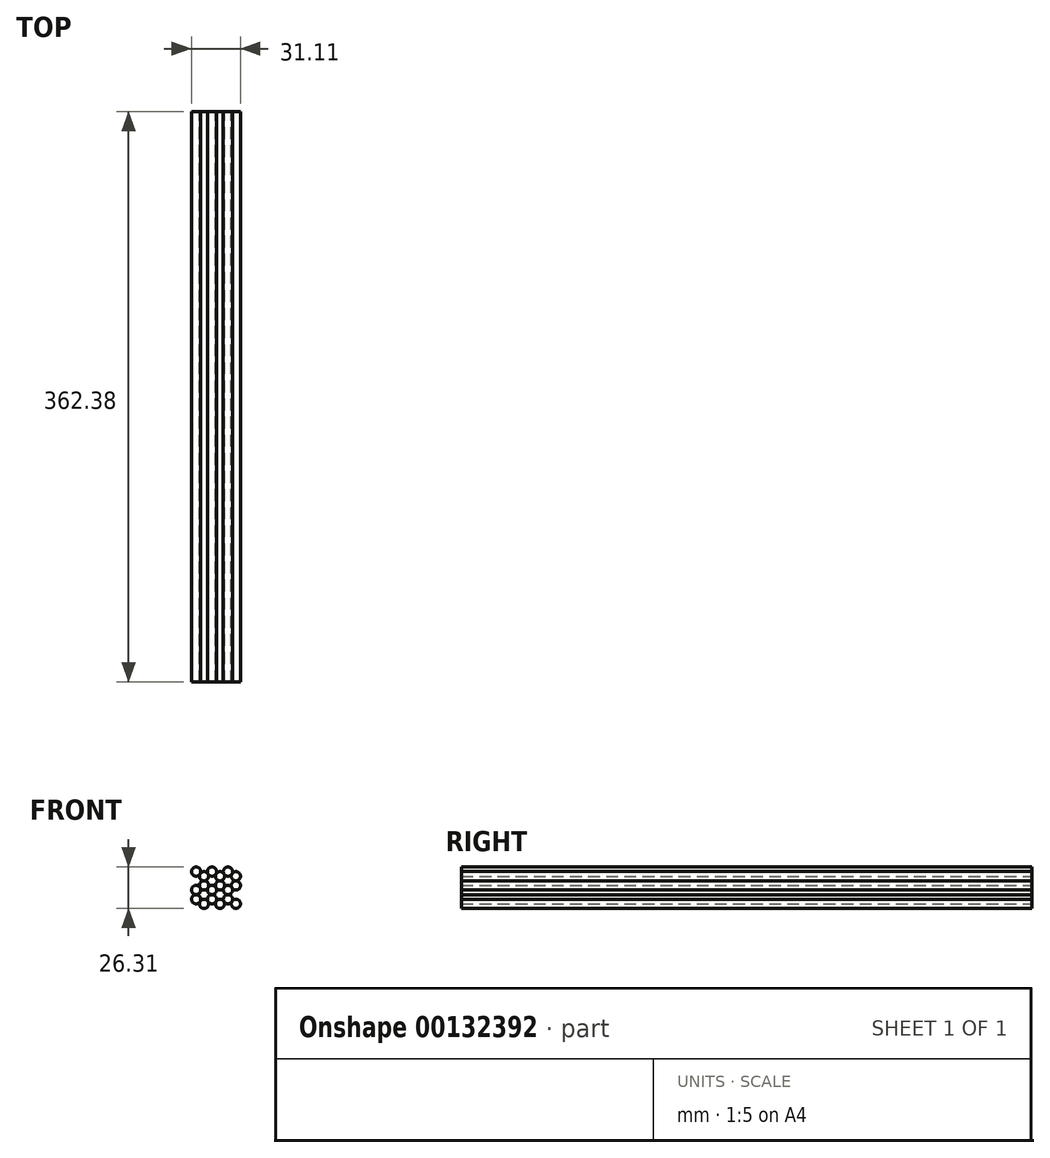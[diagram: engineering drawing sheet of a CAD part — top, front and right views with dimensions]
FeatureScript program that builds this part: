
annotation { "Feature Type Name" : "Feature", "Feature Type Description" : "" }
export const myFeature = defineFeature(function(context is Context, id is Id, definition is map)
    precondition{}
    {
        {
            var Q0;
            Q0=qCreatedBy(makeId("Front.planeOp"),FACE);
            var sketch = newSketch(context, id + "F0", { "sketchPlane" : qUnion([Q0])});
            skCircle(sketch, "E0", {"center": v(0, 0) * mm, "radius": 2.92 * mm});
            skCircle(sketch, "E1", {"center": v(5.05, -2.93) * mm, "radius": 2.92 * mm});
            skCircle(sketch, "E2", {"center": v(5.05, -8.77) * mm, "radius": 2.92 * mm});
            skCircle(sketch, "E3", {"center": v(0, -11.7) * mm, "radius": 2.92 * mm});
            skCircle(sketch, "E4", {"center": v(-5.05, -8.77) * mm, "radius": 2.92 * mm});
            skCircle(sketch, "E5", {"center": v(-5.05, -2.93) * mm, "radius": 2.92 * mm});
            skCircle(sketch, "E6", {"center": v(-10.1, 0) * mm, "radius": 2.92 * mm});
            skCircle(sketch, "E7", {"center": v(10.1, 0) * mm, "radius": 2.92 * mm});
            skCircle(sketch, "E8", {"center": v(15.16, -2.93) * mm, "radius": 2.92 * mm});
            skCircle(sketch, "E9", {"center": v(15.16, -8.77) * mm, "radius": 2.92 * mm});
            skCircle(sketch, "E10", {"center": v(10.1, -11.7) * mm, "radius": 2.92 * mm});
            skCircle(sketch, "E11", {"center": v(0, -17.54) * mm, "radius": 2.92 * mm});
            skCircle(sketch, "E12", {"center": v(-5.05, -20.47) * mm, "radius": 2.92 * mm});
            skCircle(sketch, "E13", {"center": v(-10.1, -17.54) * mm, "radius": 2.92 * mm});
            skCircle(sketch, "E14", {"center": v(-10.1, -11.7) * mm, "radius": 2.92 * mm});
            skCircle(sketch, "E15", {"center": v(5.05, -20.47) * mm, "radius": 2.92 * mm});
            skCircle(sketch, "E16", {"center": v(10.1, -17.54) * mm, "radius": 2.92 * mm});
            skCircle(sketch, "E17", {"center": v(15.16, -20.47) * mm, "radius": 2.92 * mm});
            skSolve(sketch);
        }
        {
            var Q0;
            {var subQ0=sQuery(id+"F0.wireOp",EDGE,"E2");var subQ1=makeQuery(id+"F0.imprint","INTERSECT",VERTEX,{"derivedFrom":[sQuery(id+"F0.wireOp",EDGE,"E1"),subQ0]});Q0=makeQuery(id+"F0.imprint","IMPRINT",FACE,{"disambiguationData":[TD([[makeQuery(id+"F0.imprint","IMPRINT",EDGE,{"disambiguationData":[TD([[subQ1,-1.0]])],"derivedFrom":subQ0}),1.0]])]});}
            var Q1;
            {var subQ0=sQuery(id+"F0.wireOp",EDGE,"E10");var subQ1=makeQuery(id+"F0.imprint","INTERSECT",VERTEX,{"derivedFrom":[sQuery(id+"F0.wireOp",EDGE,"E9"),subQ0]});Q1=makeQuery(id+"F0.imprint","IMPRINT",FACE,{"disambiguationData":[TD([[makeQuery(id+"F0.imprint","IMPRINT",EDGE,{"disambiguationData":[TD([[subQ1,-1.0]])],"derivedFrom":subQ0}),1.0]])]});}
            var Q2;
            {var subQ0=sQuery(id+"F0.wireOp",EDGE,"E4");var subQ1=makeQuery(id+"F0.imprint","INTERSECT",VERTEX,{"derivedFrom":[subQ0,sQuery(id+"F0.wireOp",EDGE,"E14")]});Q2=makeQuery(id+"F0.imprint","IMPRINT",FACE,{"disambiguationData":[TD([[makeQuery(id+"F0.imprint","IMPRINT",EDGE,{"disambiguationData":[TD([[subQ1,1.0]])],"derivedFrom":subQ0}),1.0]])]});}
            var Q3;
            {var subQ0=sQuery(id+"F0.wireOp",EDGE,"E15");var subQ1=makeQuery(id+"F0.imprint","INTERSECT",VERTEX,{"derivedFrom":[sQuery(id+"F0.wireOp",EDGE,"E11"),subQ0]});Q3=makeQuery(id+"F0.imprint","IMPRINT",FACE,{"disambiguationData":[TD([[makeQuery(id+"F0.imprint","IMPRINT",EDGE,{"disambiguationData":[TD([[subQ1,1.0]])],"derivedFrom":subQ0}),1.0]])]});}
            var Q4;
            {var subQ0=sQuery(id+"F0.wireOp",EDGE,"E14");var subQ1=makeQuery(id+"F0.imprint","INTERSECT",VERTEX,{"derivedFrom":[sQuery(id+"F0.wireOp",EDGE,"E4"),subQ0]});Q4=makeQuery(id+"F0.imprint","IMPRINT",FACE,{"disambiguationData":[TD([[makeQuery(id+"F0.imprint","IMPRINT",EDGE,{"disambiguationData":[TD([[subQ1,-1.0]])],"derivedFrom":subQ0}),1.0]])]});}
            var Q5;
            {var subQ0=sQuery(id+"F0.wireOp",EDGE,"E12");var subQ1=makeQuery(id+"F0.imprint","INTERSECT",VERTEX,{"derivedFrom":[sQuery(id+"F0.wireOp",EDGE,"E11"),subQ0]});Q5=makeQuery(id+"F0.imprint","IMPRINT",FACE,{"disambiguationData":[TD([[makeQuery(id+"F0.imprint","IMPRINT",EDGE,{"disambiguationData":[TD([[subQ1,-1.0]])],"derivedFrom":subQ0}),1.0]])]});}
            var Q6;
            {var subQ0=sQuery(id+"F0.wireOp",EDGE,"E11");var subQ1=makeQuery(id+"F0.imprint","INTERSECT",VERTEX,{"derivedFrom":[subQ0,sQuery(id+"F0.wireOp",EDGE,"E12")]});Q6=makeQuery(id+"F0.imprint","IMPRINT",FACE,{"disambiguationData":[TD([[makeQuery(id+"F0.imprint","IMPRINT",EDGE,{"disambiguationData":[TD([[subQ1,1.0]])],"derivedFrom":subQ0}),1.0]])]});}
            var Q7;
            Q7=makeQuery(id+"F0.imprint","IMPRINT",FACE,{"disambiguationData":[TD([[makeQuery(id+"F0.imprint","IMPRINT",EDGE,{"derivedFrom":sQuery(id+"F0.wireOp",EDGE,"E17")}),1.0]])]});
            var Q8;
            {var subQ0=sQuery(id+"F0.wireOp",EDGE,"E13");var subQ1=makeQuery(id+"F0.imprint","INTERSECT",VERTEX,{"derivedFrom":[sQuery(id+"F0.wireOp",EDGE,"E12"),subQ0]});Q8=makeQuery(id+"F0.imprint","IMPRINT",FACE,{"disambiguationData":[TD([[makeQuery(id+"F0.imprint","IMPRINT",EDGE,{"disambiguationData":[TD([[subQ1,1.0]])],"derivedFrom":subQ0}),1.0]])]});}
            var Q9;
            {var subQ0=sQuery(id+"F0.wireOp",EDGE,"E5");var subQ1=makeQuery(id+"F0.imprint","INTERSECT",VERTEX,{"derivedFrom":[subQ0,sQuery(id+"F0.wireOp",EDGE,"E6")]});Q9=makeQuery(id+"F0.imprint","IMPRINT",FACE,{"disambiguationData":[TD([[makeQuery(id+"F0.imprint","IMPRINT",EDGE,{"disambiguationData":[TD([[subQ1,1.0]])],"derivedFrom":subQ0}),1.0]])]});}
            var Q10;
            {var subQ0=sQuery(id+"F0.wireOp",EDGE,"E1");var subQ1=makeQuery(id+"F0.imprint","INTERSECT",VERTEX,{"derivedFrom":[sQuery(id+"F0.wireOp",EDGE,"E0"),subQ0]});Q10=makeQuery(id+"F0.imprint","IMPRINT",FACE,{"disambiguationData":[TD([[makeQuery(id+"F0.imprint","IMPRINT",EDGE,{"disambiguationData":[TD([[subQ1,1.0]])],"derivedFrom":subQ0}),1.0]])]});}
            var Q11;
            {var subQ0=sQuery(id+"F0.wireOp",EDGE,"E3");var subQ1=makeQuery(id+"F0.imprint","INTERSECT",VERTEX,{"derivedFrom":[sQuery(id+"F0.wireOp",EDGE,"E2"),subQ0]});Q11=makeQuery(id+"F0.imprint","IMPRINT",FACE,{"disambiguationData":[TD([[makeQuery(id+"F0.imprint","IMPRINT",EDGE,{"disambiguationData":[TD([[subQ1,-1.0]])],"derivedFrom":subQ0}),1.0]])]});}
            var Q12;
            {var subQ0=sQuery(id+"F0.wireOp",EDGE,"E8");var subQ1=makeQuery(id+"F0.imprint","INTERSECT",VERTEX,{"derivedFrom":[sQuery(id+"F0.wireOp",EDGE,"E7"),subQ0]});Q12=makeQuery(id+"F0.imprint","IMPRINT",FACE,{"disambiguationData":[TD([[makeQuery(id+"F0.imprint","IMPRINT",EDGE,{"disambiguationData":[TD([[subQ1,-1.0]])],"derivedFrom":subQ0}),1.0]])]});}
            var Q13;
            {var subQ0=sQuery(id+"F0.wireOp",EDGE,"E16");var subQ1=makeQuery(id+"F0.imprint","INTERSECT",VERTEX,{"derivedFrom":[sQuery(id+"F0.wireOp",EDGE,"E10"),subQ0]});Q13=makeQuery(id+"F0.imprint","IMPRINT",FACE,{"disambiguationData":[TD([[makeQuery(id+"F0.imprint","IMPRINT",EDGE,{"disambiguationData":[TD([[subQ1,-1.0]])],"derivedFrom":subQ0}),1.0]])]});}
            var Q14;
            {var subQ0=sQuery(id+"F0.wireOp",EDGE,"E9");var subQ1=makeQuery(id+"F0.imprint","INTERSECT",VERTEX,{"derivedFrom":[sQuery(id+"F0.wireOp",EDGE,"E8"),subQ0]});Q14=makeQuery(id+"F0.imprint","IMPRINT",FACE,{"disambiguationData":[TD([[makeQuery(id+"F0.imprint","IMPRINT",EDGE,{"disambiguationData":[TD([[subQ1,-1.0]])],"derivedFrom":subQ0}),1.0]])]});}
            var Q15;
            Q15=makeQuery(id+"F0.imprint","IMPRINT",FACE,{"disambiguationData":[TD([[makeQuery(id+"F0.imprint","IMPRINT",EDGE,{"derivedFrom":sQuery(id+"F0.wireOp",EDGE,"E6")}),1.0]])]});
            var Q16;
            {var subQ0=sQuery(id+"F0.wireOp",EDGE,"E0");var subQ1=makeQuery(id+"F0.imprint","INTERSECT",VERTEX,{"derivedFrom":[subQ0,sQuery(id+"F0.wireOp",EDGE,"E1")]});Q16=makeQuery(id+"F0.imprint","IMPRINT",FACE,{"disambiguationData":[TD([[makeQuery(id+"F0.imprint","IMPRINT",EDGE,{"disambiguationData":[TD([[subQ1,1.0]])],"derivedFrom":subQ0}),1.0]])]});}
            var Q17;
            {var subQ0=sQuery(id+"F0.wireOp",EDGE,"E7");var subQ1=makeQuery(id+"F0.imprint","INTERSECT",VERTEX,{"derivedFrom":[sQuery(id+"F0.wireOp",EDGE,"E1"),subQ0]});Q17=makeQuery(id+"F0.imprint","IMPRINT",FACE,{"disambiguationData":[TD([[makeQuery(id+"F0.imprint","IMPRINT",EDGE,{"disambiguationData":[TD([[subQ1,-1.0]])],"derivedFrom":subQ0}),1.0]])]});}
            extrude(context, id + "F1", {"entities" : qUnion([Q0, Q1, Q2, Q3, Q4, Q5, Q6, Q7, Q8, Q9, Q10, Q11, Q12, Q13, Q14, Q15, Q16, Q17]), "depth" : 362.38 * mm});
        }
    });
